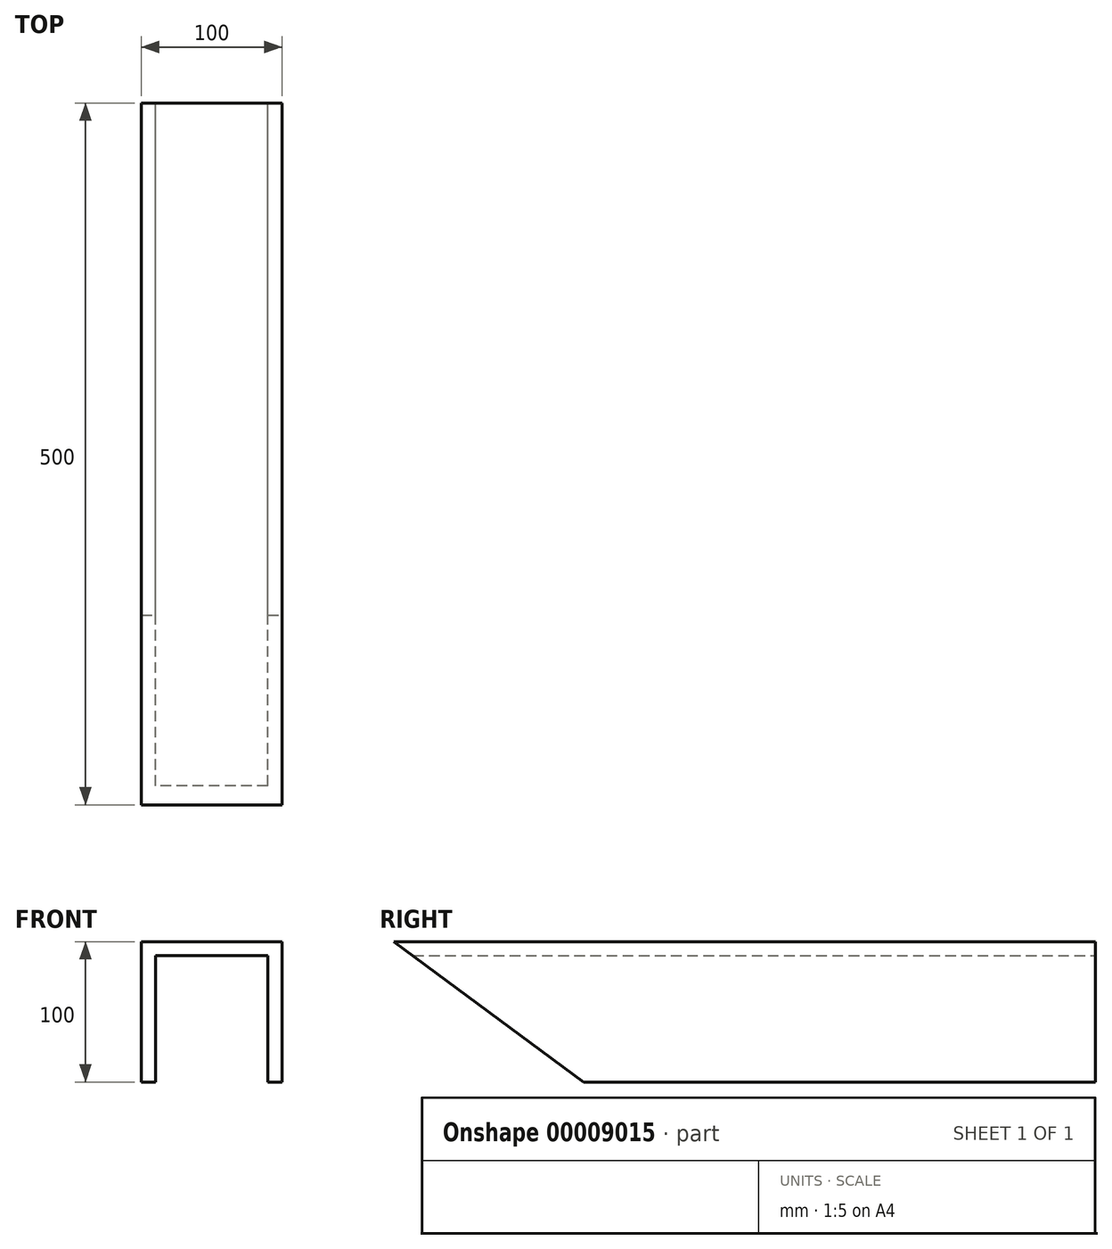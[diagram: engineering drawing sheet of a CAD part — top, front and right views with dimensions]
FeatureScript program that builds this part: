
annotation { "Feature Type Name" : "Feature", "Feature Type Description" : "" }
export const myFeature = defineFeature(function(context is Context, id is Id, definition is map)
    precondition{}
    {
        {
            var Q0;
            Q0=qCreatedBy(makeId("Front.planeOp"),FACE);
            var sketch = newSketch(context, id + "F0", { "sketchPlane" : qUnion([Q0])});
            skLineSegment(sketch, "E0.rect.bottom", {"start": v(50, 100) * mm, "end": v(-50, 100) * mm});
            skLineSegment(sketch, "E0.rect.left", {"start": v(50, 100) * mm, "end": v(50, 0) * mm});
            skLineSegment(sketch, "E0.rect.right", {"start": v(-50, 100) * mm, "end": v(-50, 0) * mm});
            skPoint(sketch, "E0.rect.middle", {"position": v(0, 0) * mm});
            skLineSegment(sketch, "E1.rect.bottom", {"start": v(40, 90) * mm, "end": v(-40, 90) * mm});
            skLineSegment(sketch, "E1.rect.left", {"start": v(40, 90) * mm, "end": v(40, 0) * mm});
            skLineSegment(sketch, "E1.rect.right", {"start": v(-40, 90) * mm, "end": v(-40, 0) * mm});
            skLineSegment(sketch, "E2", {"start": v(-50, 0) * mm, "end": v(-40, 0) * mm});
            skLineSegment(sketch, "E3", {"start": v(40, 0) * mm, "end": v(50, 0) * mm});
            skPoint(sketch, "E1.rect.top.end.orphan", {"position": v(-40, -90) * mm});
            skPoint(sketch, "E1.rect.top.start.orphan", {"position": v(40, -90) * mm});
            skPoint(sketch, "E0.rect.top.end.orphan", {"position": v(-50, -100) * mm});
            skPoint(sketch, "E0.rect.top.start.orphan", {"position": v(50, -100) * mm});
            skSolve(sketch);
        }
        {
            var Q0;
            Q0=qSketchRegion(id+"F0",true);
            extrude(context, id + "F1", {"entities" : qUnion([Q0]), "endBound" : BoundingType.SYMMETRIC, "depth" : 500 * mm});
        }
        {
            var Q0;
            Q0=makeQuery(id+"F1.opExtrude","SWEPT_FACE",FACE,{"disambiguationData":[OSD([sQuery(id+"F0.wireOp",EDGE,"E0.rect.left")])]});
            var sketch = newSketch(context, id + "F2", { "sketchPlane" : qUnion([Q0])});
            skLineSegment(sketch, "E4", {"start": v(-250, 100) * mm, "end": v(-115, 0) * mm});
            skSolve(sketch);
        }
        {
            var Q0;
            {var subQ2=sQuery(id+"F2.wireOp",EDGE,"E4");Q0=makeQuery(id+"F2.imprint","IMPRINT",FACE,{"disambiguationData":[TD([[makeQuery(id+"F2.imprint","IMPRINT",EDGE,{"derivedFrom":subQ2}),-1.0]])]});}
            extrude(context, id + "F3", {"entities" : qUnion([Q0]), "operationType" : NewBodyOperationType.REMOVE, "endBound" : BoundingType.THROUGH_ALL, "oppositeDirection" : true, "depth" : 25 * mm});
        }
    });
